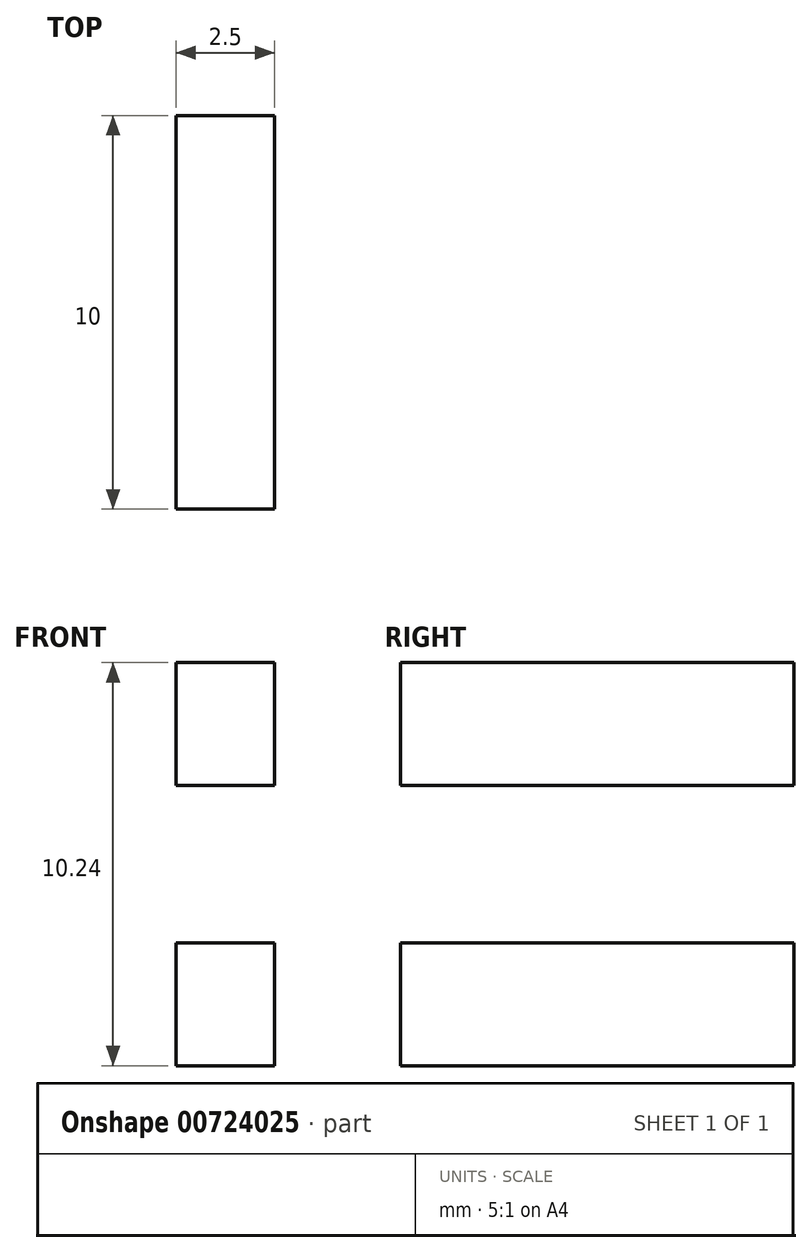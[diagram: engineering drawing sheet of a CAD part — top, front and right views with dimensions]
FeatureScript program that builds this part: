
annotation { "Feature Type Name" : "Feature", "Feature Type Description" : "" }
export const myFeature = defineFeature(function(context is Context, id is Id, definition is map)
    precondition{}
    {
        {
            var Q0;
            Q0=qCreatedBy(makeId("Right.planeOp"),FACE);
            var sketch = newSketch(context, id + "F0", { "sketchPlane" : qUnion([Q0])});
            skLineSegment(sketch, "E0.left", {"start": v(0, 0) * mm, "end": v(0, 3) * mm});
            skLineSegment(sketch, "E0.right", {"start": v(-10, 0) * mm, "end": v(-10, 3) * mm});
            skLineSegment(sketch, "E1", {"start": v(0, 10) * mm, "end": v(0, 7) * mm});
            skLineSegment(sketch, "E2", {"start": v(0, 7) * mm, "end": v(-8, 7) * mm});
            skLineSegment(sketch, "E3.MirrorCS", {"start": v(0, 3) * mm, "end": v(-8, 3) * mm});
            skLineSegment(sketch, "E4", {"start": v(0, 0) * mm, "end": v(0, -0.13) * mm});
            skLineSegment(sketch, "E5", {"start": v(0, 10) * mm, "end": v(0, 10.12) * mm});
            skLineSegment(sketch, "E6", {"start": v(0, 10.12) * mm, "end": v(-10, 10.12) * mm});
            skLineSegment(sketch, "E7", {"start": v(-10, 10.12) * mm, "end": v(-10, 10) * mm});
            skLineSegment(sketch, "E8", {"start": v(0, -0.13) * mm, "end": v(-10, -0.13) * mm});
            skLineSegment(sketch, "E9", {"start": v(-10, -0.13) * mm, "end": v(-10, 0) * mm});
            skPoint(sketch, "E10.orphan", {"position": v(-10, 5) * mm});
            skPoint(sketch, "E11.end.orphan", {"position": v(0, 5) * mm});
            skLineSegment(sketch, "E12", {"start": v(-8, 7) * mm, "end": v(-10, 7) * mm});
            skLineSegment(sketch, "E13", {"start": v(-8, 3) * mm, "end": v(-10, 3) * mm});
            skLineSegment(sketch, "E14.trimOffspring", {"start": v(-10, 7) * mm, "end": v(-10, 10) * mm});
            skSolve(sketch);
        }
        {
            var Q0;
            Q0=makeQuery(id+"F0.imprint","IMPRINT",FACE,{"disambiguationData":[TD([[makeQuery(id+"F0.imprint","IMPRINT",EDGE,{"derivedFrom":sQuery(id+"F0.wireOp",EDGE,"E0.left")}),1.0]])]});
            var Q1;
            Q1=makeQuery(id+"F0.imprint","IMPRINT",FACE,{"disambiguationData":[TD([[makeQuery(id+"F0.imprint","IMPRINT",EDGE,{"derivedFrom":sQuery(id+"F0.wireOp",EDGE,"E1")}),-1.0]])]});
            extrude(context, id + "F1", {"entities" : qUnion([Q0, Q1]), "depth" : 2.5 * mm, "offsetDistance" : 25 * mm});
        }
    });
